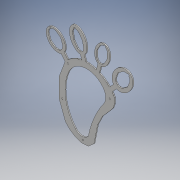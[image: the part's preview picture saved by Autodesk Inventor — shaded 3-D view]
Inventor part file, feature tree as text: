
AUTODESK INVENTOR PART (.ipt)
format: ipt  version: 2018 (Build 220112000, 112)  size: 254,976 bytes
history: native  units: mm
features: extrude x1, sketch x1
ambient origin geometry x8: Origin, YZ Plane, XZ Plane, XY Plane, X Axis, Y Axis, Z Axis, Center Point
bodies: Solid1 (feature_tree)
feature tree (2):
  extrude  "Extrusion1"  Depth=1.0mm TaperAngle=0.0deg
  sketch  "Sketch1"  dims[d0=1.5mm d1=2.0mm d2=2.0mm d3=2.0mm d4=2.0mm d5=1.5mm d6=1.5mm d7=1.5mm d8=1.0mm d9=0.0mm]
